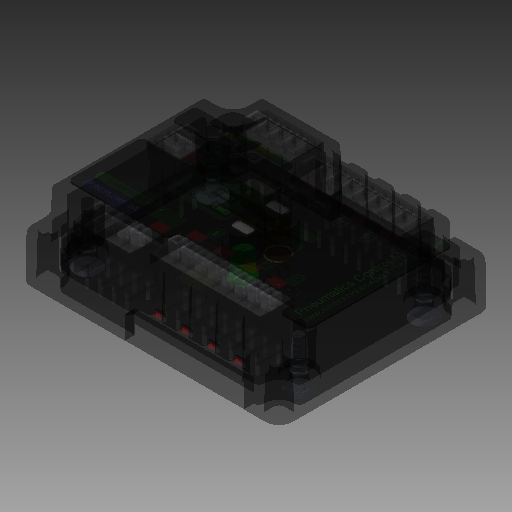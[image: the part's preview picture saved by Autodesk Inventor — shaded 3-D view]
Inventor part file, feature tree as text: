
AUTODESK INVENTOR PART (.ipt)
format: ipt  version: 2019 (Build 230136000, 136)  size: 12,993,024 bytes
history: native  units: in
note: dims shown in document units (in); Inventor stores cm internally (conversion verified against a paired STEP export)
features: other x3, sketch x1
ambient origin geometry x8: Origin, YZ Plane, XZ Plane, XY Plane, X Axis, Y Axis, Z Axis, Center Point
bodies: Body1 (feature_tree), Body2 (feature_tree), Body3 (feature_tree), Body4 (feature_tree), Body5 (feature_tree), Body6 (feature_tree), Body7 (feature_tree), Body8 (feature_tree), Body9 (feature_tree), Body10 (feature_tree), Body11 (feature_tree), Body12 (feature_tree), Body13 (feature_tree), Body14 (feature_tree), Body15 (feature_tree), Body16 (feature_tree), Body17 (feature_tree), Body18 (feature_tree), Body19 (feature_tree), Body20 (feature_tree), Body21 (feature_tree), Body22 (feature_tree), Body23 (feature_tree), Body24 (feature_tree)
feature tree (4):
  other  "pneumatic control1"
  sketch  "Sketch1"  dims[d0=1.923in d1=2.403in]
  other  "Composite1"
  other  "Srf1"
